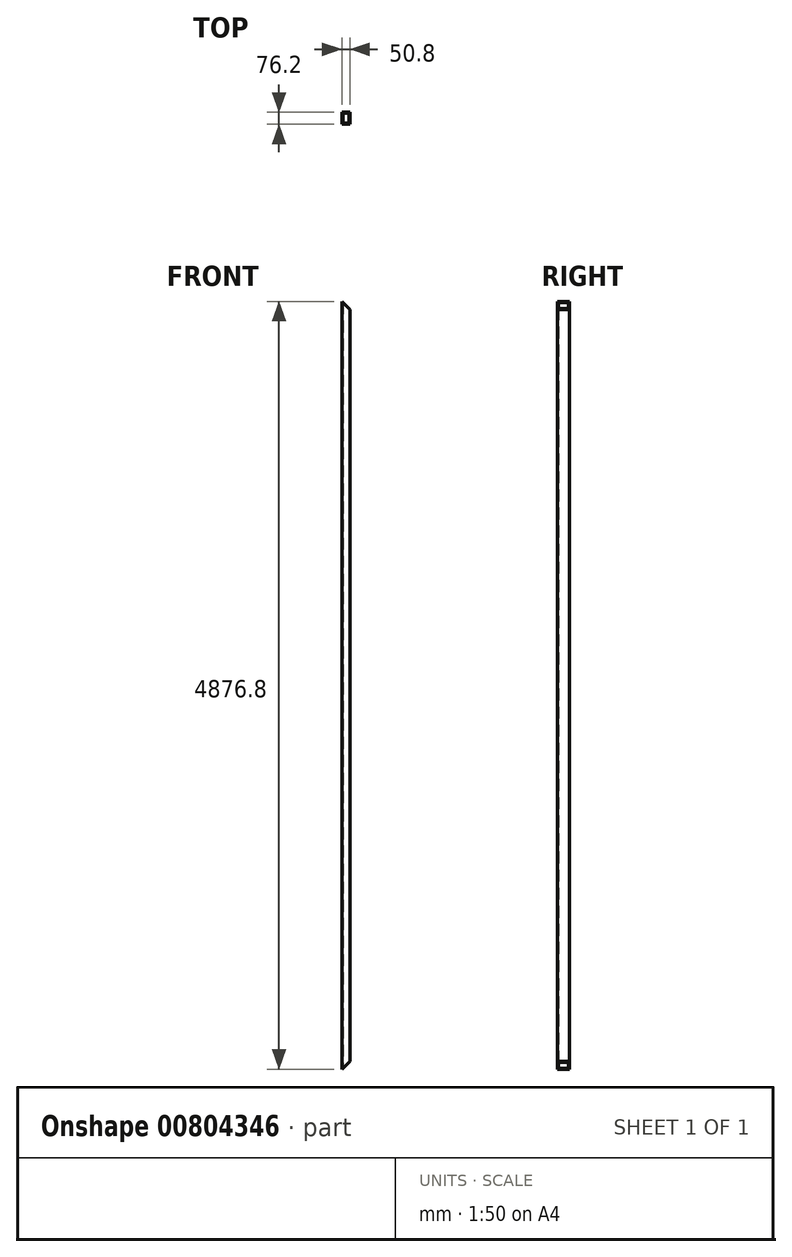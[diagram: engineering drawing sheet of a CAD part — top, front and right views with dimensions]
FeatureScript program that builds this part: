
annotation { "Feature Type Name" : "Feature", "Feature Type Description" : "" }
export const myFeature = defineFeature(function(context is Context, id is Id, definition is map)
    precondition{}
    {
        {
            var Q0;
            Q0=qCreatedBy(makeId("Top.planeOp"),FACE);
            var sketch = newSketch(context, id + "F0", { "sketchPlane" : qUnion([Q0])});
            skLineSegment(sketch, "E0.bottom", {"start": v(25.4, -38.1) * mm, "end": v(-25.4, -38.1) * mm});
            skLineSegment(sketch, "E0.top", {"start": v(25.4, 38.1) * mm, "end": v(-25.4, 38.1) * mm});
            skLineSegment(sketch, "E0.left", {"start": v(25.4, -38.1) * mm, "end": v(25.4, 38.1) * mm});
            skLineSegment(sketch, "E0.right", {"start": v(-25.4, -38.1) * mm, "end": v(-25.4, 38.1) * mm});
            skPoint(sketch, "E0.middle", {"position": v(0, 0) * mm});
            skLineSegment(sketch, "E1.0", {"start": v(19.05, -31.75) * mm, "end": v(-19.05, -31.75) * mm});
            skLineSegment(sketch, "E1.1", {"start": v(19.05, -31.75) * mm, "end": v(19.05, 31.75) * mm});
            skLineSegment(sketch, "E1.2", {"start": v(19.05, 31.75) * mm, "end": v(-19.05, 31.75) * mm});
            skLineSegment(sketch, "E1.3", {"start": v(-19.05, -31.75) * mm, "end": v(-19.05, 31.75) * mm});
            skSolve(sketch);
        }
        {
            var Q0;
            Q0=makeQuery(id+"F0.imprint","IMPRINT",FACE,{"disambiguationData":[TD([[makeQuery(id+"F0.imprint","IMPRINT",EDGE,{"derivedFrom":sQuery(id+"F0.wireOp",EDGE,"E0.bottom")}),-1.0]])]});
            extrude(context, id + "F1", {"entities" : qUnion([Q0]), "depth" : 4876.8 * mm, "offsetDistance" : 25.4 * mm});
        }
        {
            var Q0;
            Q0=makeQuery(id+"F1.opExtrude","SWEPT_FACE",FACE,{"disambiguationData":[OSD([sQuery(id+"F0.wireOp",EDGE,"E0.bottom")])]});
            var sketch = newSketch(context, id + "F2", { "sketchPlane" : qUnion([Q0])});
            skLineSegment(sketch, "E2", {"start": v(-25.4, 0) * mm, "end": v(25.4, 50.8) * mm});
            skLineSegment(sketch, "E3", {"start": v(-25.4, 4876.8) * mm, "end": v(25.4, 4826) * mm});
            skSolve(sketch);
        }
        {
            var Q0;
            {var subQ0=sQuery(id+"F2.wireOp",EDGE,"E2");Q0=makeQuery(id+"F2.imprint","IMPRINT",FACE,{"disambiguationData":[TD([[makeQuery(id+"F2.imprint","IMPRINT",EDGE,{"derivedFrom":subQ0}),-1.0]])]});}
            var Q1;
            {var subQ0=sQuery(id+"F2.wireOp",EDGE,"E3");Q1=makeQuery(id+"F2.imprint","IMPRINT",FACE,{"disambiguationData":[TD([[makeQuery(id+"F2.imprint","IMPRINT",EDGE,{"derivedFrom":subQ0}),1.0]])]});}
            extrude(context, id + "F3", {"entities" : qUnion([Q0, Q1]), "operationType" : NewBodyOperationType.REMOVE, "oppositeDirection" : true, "depth" : 76.2 * mm, "offsetDistance" : 25.4 * mm});
        }
    });
